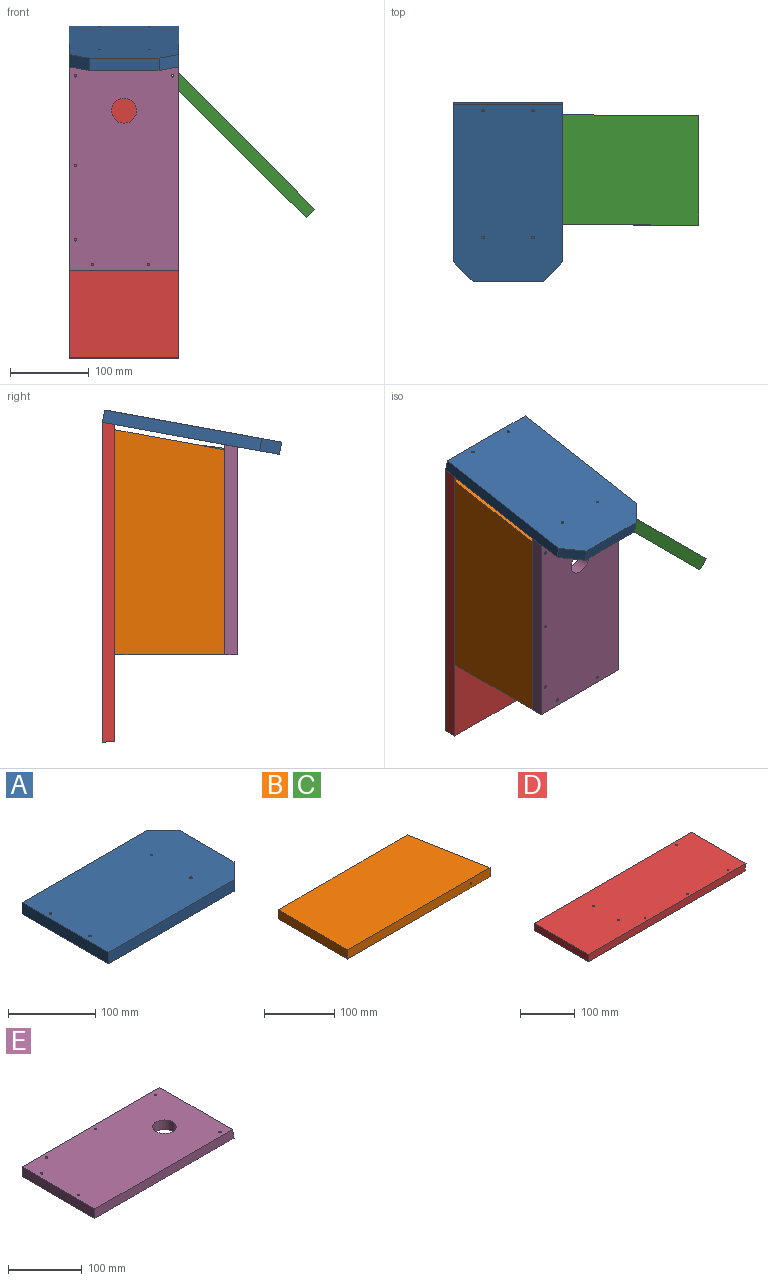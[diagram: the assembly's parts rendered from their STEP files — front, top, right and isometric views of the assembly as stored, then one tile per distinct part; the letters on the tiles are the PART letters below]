
ASSEMBLY  parts=5 mates=4
PART A: 12 faces, bbox 228.6x139.7x15.9 mm
  f0: plane 203.2x15.88mm, normal (0,1,0), area 3225.8mm2, adj f1,f8,f10,f11
  f1: plane 139.7x15.88mm, normal (-1,0,0), area 2217.7mm2, adj f0,f2,f10,f11
  f2: plane 203.2x15.88mm, normal (0,-1,0), area 3225.8mm2, adj f1,f3,f10,f11
  f3: plane 25.4x25.4mm, normal (0.71,-0.71,0), area 570.2mm2, adj f2,f4,f10,f11
  f4: plane 88.9x15.88mm, normal (1,0,0), area 1411.3mm2, adj f3,f8,f10,f11
  f5: cylinder r=1.59mm len=15.88mm, axis (0,0,-1), area 158.3mm2, adj f10,f11
  f6: cylinder r=1.59mm len=15.88mm, axis (0,0,-1), area 158.3mm2, adj f10,f11
  f7: cylinder r=1.59mm len=15.88mm, axis (0,0,-1), area 158.3mm2, adj f10,f11
  f8: plane 25.4x25.4mm, normal (0.71,0.71,0), area 570.2mm2, adj f0,f4,f10,f11
  f9: cylinder r=1.59mm len=15.88mm, axis (0,0,-1), area 158.3mm2, adj f10,f11
  f10: plane 228.6x139.7mm, normal (0,0,1), area 31258.6mm2, adj f0,f1,f2,f3,f4,f5,f6,f7
  f11: plane 228.6x139.7mm, normal (0,0,-1), area 31258.6mm2, adj f0,f1,f2,f3,f4,f5,f6,f7
PART B: 7 faces, bbox 285.8x139.7x15.9 mm
  f0: plane 260.35x15.88mm, normal (0,1,0), area 4125.1mm2, adj f1,f3,f4,f5,f6
  f1: plane 139.7x15.88mm, normal (-1,0,0), area 2217.7mm2, adj f0,f2,f4,f5
  f2: plane 285.75x15.88mm, normal (0,-1,0), area 4528.4mm2, adj f1,f3,f4,f5,f6
  f3: plane 139.7x25.4mm, normal (0.98,0.18,0), area 2254.1mm2, adj f0,f2,f4,f5
  f4: plane 285.75x139.7mm, normal (0,0,1), area 38145.1mm2, adj f0,f1,f2,f3
  f5: plane 285.75x139.7mm, normal (0,0,-1), area 38145.1mm2, adj f0,f1,f2,f3
  f6: cylinder r=1.59mm len=139.7mm, axis (0,1,0), area 1393.4mm2, adj f0,f2
PART C: same geometry as B
PART D: 12 faces, bbox 406.4x139.7x15.9 mm
  f0: plane 139.7x15.88mm, normal (-1,0,0), area 2217.7mm2, adj f1,f8,f10,f11
  f1: plane 406.4x15.88mm, normal (0,-1,0), area 6428.7mm2, adj f0,f2,f10,f11
  f2: plane 139.7x15.88mm, normal (0.98,0,-0.18), area 2254.1mm2, adj f1,f8,f10,f11
  f3: cylinder r=1.59mm len=15.88mm, axis (0,0,-1), area 158.3mm2, adj f10,f11
  f4: cylinder r=1.59mm len=15.88mm, axis (0,0,-1), area 158.3mm2, adj f10,f11
  f5: cylinder r=1.59mm len=15.88mm, axis (0,0,-1), area 158.3mm2, adj f10,f11
  f6: cylinder r=1.59mm len=15.88mm, axis (0,0,-1), area 158.3mm2, adj f10,f11
  f7: cylinder r=1.59mm len=15.88mm, axis (0,0,-1), area 158.3mm2, adj f10,f11
  f8: plane 406.4x15.88mm, normal (0,1,0), area 6428.7mm2, adj f0,f2,f10,f11
  f9: cylinder r=1.59mm len=15.88mm, axis (0,0,-1), area 158.3mm2, adj f10,f11
  f10: plane 406.4x139.7mm, normal (0,0,1), area 56726.6mm2, adj f0,f1,f2,f3,f4,f5,f6,f7
  f11: plane 403.52x139.7mm, normal (0,0,-1), area 56323.5mm2, adj f0,f1,f2,f3,f4,f5,f6,f7
PART E: 13 faces, bbox 266.7x139.7x15.9 mm
  f0: plane 266.7x15.88mm, normal (0,1,0), area 4211mm2, adj f1,f10,f11,f12
  f1: plane 139.7x15.88mm, normal (-1,0,0), area 2217.7mm2, adj f0,f2,f11,f12
  f2: plane 266.7x15.88mm, normal (0,-1,0), area 4211mm2, adj f1,f10,f11,f12
  f3: cylinder r=15.88mm len=31.75mm, axis (0,0,-1), area 1583.5mm2, adj f11,f12
  f4: cylinder r=1.59mm len=15.88mm, axis (0,0,-1), area 158.3mm2, adj f11,f12
  f5: cylinder r=1.59mm len=15.88mm, axis (0,0,-1), area 158.3mm2, adj f11,f12
  f6: cylinder r=1.59mm len=15.88mm, axis (0,0,-1), area 158.3mm2, adj f11,f12
  f7: cylinder r=1.59mm len=15.88mm, axis (0,0,-1), area 158.3mm2, adj f11,f12
  f8: cylinder r=1.59mm len=15.88mm, axis (0,0,-1), area 158.3mm2, adj f11,f12
  f9: cylinder r=1.59mm len=15.88mm, axis (0,0,-1), area 158.3mm2, adj f11,f12
  f10: plane 139.7x15.88mm, normal (0.98,0,0.18), area 2254.1mm2, adj f0,f2,f11,f12
  f11: plane 263.82x139.7mm, normal (0,0,1), area 36015.7mm2, adj f0,f1,f2,f3,f4,f5,f6,f7
  f12: plane 266.7x139.7mm, normal (0,0,-1), area 36418.8mm2, adj f0,f1,f2,f3,f4,f5,f6,f7
PLACE A rot(axis=(0.09,0.09,-0.99),90.5deg) t=(-715.34,402.36,275.33)mm
PLACE B rot(axis=(0.71,0,0.71),180deg) t=(-945.26,-123.85,-82.36)mm
PLACE C rot(axis=(0.38,0,0.92),180deg) t=(-643.99,-123.85,-15.44)mm
PLACE D rot(axis=(-0.58,-0.58,-0.58),120deg) t=(-953.48,43,-324.58)mm
PLACE E rot(axis=(0.58,-0.58,0.58),120deg) t=(-1137.13,-96.7,-88.5)mm
MATE fastened D.f2 <-> A.f11  axis (0,-0.18,0.98) through (-945.26,58.87,212.91)mm
MATE revolute E.f4 <-> C.f6  axis (0,1,0) through (-813.5,-96.7,165.29)mm
MATE fastened B.f0 <-> E.f12  axis (0,-1,0) through (-945.26,-96.7,177.99)mm
MATE fastened D.f11 <-> B.f2  axis (0,-1,0) through (-945.26,43,-193.49)mm
